# Revit family: Doors_Industrial_Overhead-Door-Corporation_ProStar-Rolling-Steel-Sheet-Doors-790CW_
name_source: partatom
category: Specialty Equipment
units: mm (PartAtom-declared; Revit-internal decimal feet)

## family parameters
Always vertical = Yes
Cut with Voids When Loaded = No
Host = Wall
OmniClass Number = 23.30.10.21.34
OmniClass Title = Industrial Doors
Part Type = Normal
Room Calculation Point = No
Round Connector Dimension = Use Diameter
Shared = No

## types (5) — shared parameters
Description = MODEL 790CW COMMERCIAL WINDLOAD SHEET DOOR
Finish Material = Metal - Overhead Door - Galvanized Steel
Manufacturer = Overhead Door Corporation
Model = 790CW
Number of Poles = 1
Power Factor = 1
Product Guid = 31ea9244-d163-47bf-8a72-29b8d9e5b7aa
Product Page URL = https://www.overheaddoor.com
Product data url = https://www.bimobject.com
Slat Height = 10"
URL = https://www.overheaddoor.com
Wall Closure = By host

## per-type parameters (varying)
| type | Apparent Load Phase 1 | Current | Electrical Operator | Frequency | Voltage |
| ‏​Manual push-up | 0 VA | 0 A | No | 0 Hz | 0 V |
| Chain Hoist | 0 VA | 0 A | No | 0 Hz | 0 V |
| 115 volts, one phase, 60 Hz (110-120V range) | 2300 VA | 20 A | Yes | 60 Hz | 115 V |
| 208 volts, one phase, 60 Hz (190-207V range) | 4160 VA | 20 A | Yes | 60 Hz | 208 V |
| 230 volts, one phase, 60 Hz (208-245V range) | 4600 VA | 20 A | Yes | 60 Hz | 230 V |

type visibility flags (boolean, named after types; folded from table):
- ‏​Manual push-up: Yes: (none)
- Chain Hoist: Yes: Chain Hoist
- 115 volts, one phase, 60 Hz (110-120V range): Yes: (none)
- 208 volts, one phase, 60 Hz (190-207V range): Yes: (none)
- 230 volts, one phase, 60 Hz (208-245V range): Yes: (none)

## geometry (parser evidence)
native form markers: Sweep x8
no freeform markers — native parametric forms only
